# Revit family: Truck-Shelter_m500_Marvel-Equipment
name_source: partatom
category: Doors
units: mm (PartAtom-declared; Revit-internal decimal feet)

## family parameters
Always vertical = Yes
Cut with Voids When Loaded = No
Host = Wall
OmniClass Number = 23.30.10.00
OmniClass Title = Doors
Room Calculation Point = No
Shared = No

## types (1)
- M500
    Analytic Construction = <None>
    CAD Details = https://www.arcat.com
    Define Thermal Properties by = Schematic Type
    Function = Interior
    Header Height = 3' - 0"
    Height = 7' - 8"
    Keynote = 11 13 00
    Main Material = Black Seal / Shelter
    Manufacturer = Marvel Equipment
    Material Name = Polished
    Max. Height = 15' - 0"
    Max. Width = 15' - 0"
    Model = M500
    Overall Height = 10' - 8"
    Overall Width = 11' - 6"
    Pleat Exposure = 1' - 1 1/2"
    Product Page URL = https://www.arcat.com
    Secondary Material = -
    Side Width = 2' - 0"
    Specification = https://www.arcat.com
    URL = https://www.marvelequipmentcorp.com
    Wall Closure = By host
    Width = 7' - 6"

## geometry (parser evidence)
native form markers: Sweep x51
no freeform markers — native parametric forms only
